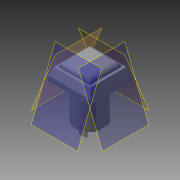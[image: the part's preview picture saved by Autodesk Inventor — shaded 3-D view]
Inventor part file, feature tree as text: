
AUTODESK INVENTOR PART (.ipt)
format: ipt  version: 2016 (Build 200138000, 138)  size: 209,920 bytes
history: native  units: in
note: dims shown in document units (in); Inventor stores cm internally (conversion verified against a paired STEP export)
features: extrude x10, sketch x10, plane x4, fillet x2
ambient origin geometry x8: Origin, YZ Plane, XZ Plane, XY Plane, X Axis, Y Axis, Z Axis, Center Point
bodies: Solid1 (feature_tree)
feature tree (26):
  extrude  "Extrusion1"  Depth=0.2165in
  extrude  "Extrusion2"  Depth=0.4961in
  extrude  "Extrusion3"  Depth=0.063in TaperAngle=0.0deg
  extrude  "Extrusion4"  Depth=0.685in
  plane  "Work Plane1"
  plane  "Work Plane2"
  plane  "Work Plane3"
  plane  "Work Plane4"
  extrude  "Extrusion5"  Depth=0.1063in
  extrude  "Extrusion6"  Depth=0.0787in
  extrude  "Extrusion7"  Depth=0.0472in
  extrude  "Extrusion8"  Depth=0.1181in TaperAngle=0.0deg
  fillet  "Fillet1"  Radius=0.1181in
  extrude  "Extrusion9"  Depth=0.1181in TaperAngle=0.0deg
  fillet  "Fillet2"  Radius=0.1181in
  extrude  "Extrusion10"  Depth=0.1575in
  sketch  "Sketch1"  dims[d0=0.4646in d1=0.2165in]
  sketch  "Sketch2"  dims[d2=0.4961in d3=0.0in d4=0.5276in]
  sketch  "Sketch3"  dims[d5=0.2362in d6=0.063in d7=0.0in]
  sketch  "Sketch4"  dims[d8=0.685in d9=0.685in]
  sketch  "Sketch5"  dims[d10=0.1063in d11=0.3425in]
  sketch  "Sketch6"  dims[d12=0.0787in d13=0.0in d14=0.5906in]
  sketch  "Sketch7"  dims[d15=0.5906in d16=0.0472in]
  sketch  "Sketch8"  dims[d17=0.0472in d18=0.1181in d19=0.0in d20=0.1181in d21=0.0in]
  sketch  "Sketch9"  dims[d22=0.1181in d23=0.0in d24=0.1181in d25=0.0in d26=0.1181in d27=0.0in]
  sketch  "Sketch10"  dims[d28=0.0197in d31=0.0394in d32=0.0394in d34=0.0394in d35=0.0394in d36=0.0787in d37=0.0in d38=0.0709in d39=0.1181in d40=0.0197in d41=0.1457in d42=0.1181in d43=0.1575in d44=0.0in]
